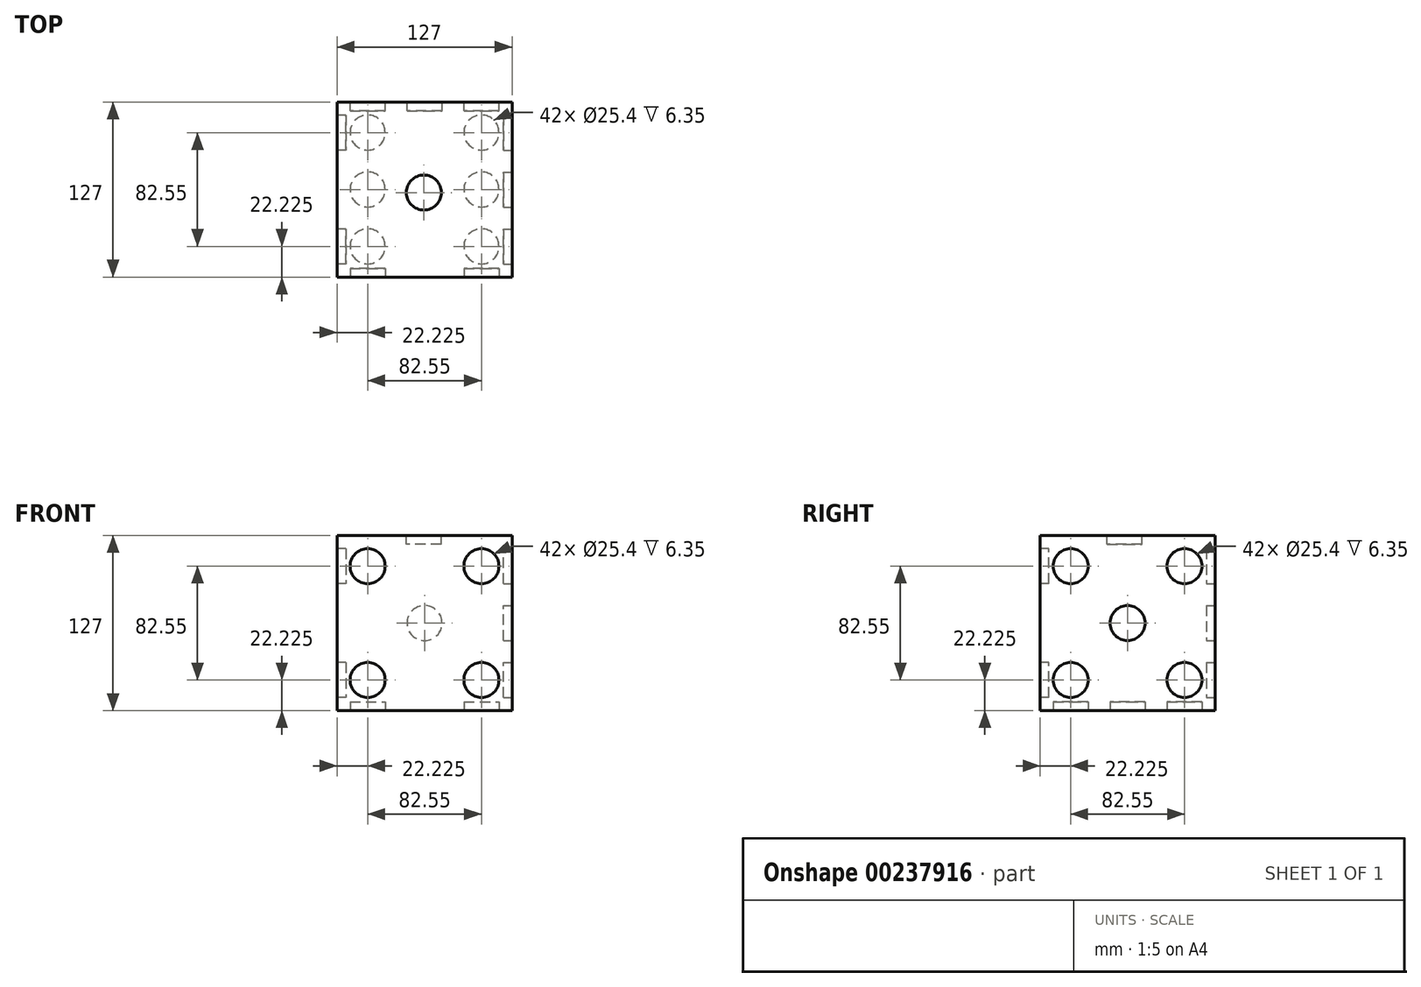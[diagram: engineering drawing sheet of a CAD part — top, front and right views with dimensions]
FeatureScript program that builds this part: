
annotation { "Feature Type Name" : "Feature", "Feature Type Description" : "" }
export const myFeature = defineFeature(function(context is Context, id is Id, definition is map)
    precondition{}
    {
        {
            var Q0;
            Q0=qCreatedBy(makeId("Top.planeOp"),FACE);
            var sketch = newSketch(context, id + "F0", { "sketchPlane" : qUnion([Q0])});
            skLineSegment(sketch, "E0.bottom", {"start": v(0, 0) * mm, "end": v(127, 0) * mm});
            skLineSegment(sketch, "E0.top", {"start": v(0, 127) * mm, "end": v(127, 127) * mm});
            skLineSegment(sketch, "E0.left", {"start": v(0, 0) * mm, "end": v(0, 127) * mm});
            skLineSegment(sketch, "E0.right", {"start": v(127, 0) * mm, "end": v(127, 127) * mm});
            skSolve(sketch);
        }
        {
            var Q0;
            Q0=makeQuery(id+"F0.imprint","IMPRINT",FACE,{"disambiguationData":[TD([[makeQuery(id+"F0.imprint","IMPRINT",EDGE,{"derivedFrom":sQuery(id+"F0.wireOp",EDGE,"E0.bottom")}),1.0]])]});
            extrude(context, id + "F1", {"entities" : qUnion([Q0]), "depth" : 127 * mm});
        }
        {
            var Q0;
            Q0=makeQuery(id+"F1.opExtrude","CAP_FACE",FACE,{"disambiguationData":[OSD([sQuery(id+"F0.wireOp",EDGE,"E0.bottom"),sQuery(id+"F0.wireOp",EDGE,"E0.top"),sQuery(id+"F0.wireOp",EDGE,"E0.left"),sQuery(id+"F0.wireOp",EDGE,"E0.right")])],"isStart":false});
            var sketch = newSketch(context, id + "F2", { "sketchPlane" : qUnion([Q0])});
            skCircle(sketch, "E1", {"center": v(63, 61.25) * mm, "radius": 12.7 * mm});
            skSolve(sketch);
        }
        {
            var Q0;
            Q0=makeQuery(id+"F2.imprint","IMPRINT",FACE,{"disambiguationData":[TD([[makeQuery(id+"F2.imprint","IMPRINT",EDGE,{"derivedFrom":sQuery(id+"F2.wireOp",EDGE,"E1")}),1.0]])]});
            extrude(context, id + "F3", {"entities" : qUnion([Q0]), "operationType" : NewBodyOperationType.REMOVE, "oppositeDirection" : true, "depth" : 6.35 * mm});
        }
        {
            var Q0;
            Q0=makeQuery(id+"F1.opExtrude","CAP_FACE",FACE,{"disambiguationData":[OSD([sQuery(id+"F0.wireOp",EDGE,"E0.bottom"),sQuery(id+"F0.wireOp",EDGE,"E0.top"),sQuery(id+"F0.wireOp",EDGE,"E0.left"),sQuery(id+"F0.wireOp",EDGE,"E0.right")])],"isStart":true});
            var sketch = newSketch(context, id + "F4", { "sketchPlane" : qUnion([Q0])});
            skLineSegment(sketch, "E2", {"start": v(63.5, 0) * mm, "end": v(63.5, -127) * mm, "construction": true});
            skLineSegment(sketch, "E3", {"start": v(0, -63.5) * mm, "end": v(127, -63.5) * mm, "construction": true});
            skCircle(sketch, "E4", {"center": v(22.23, -22.23) * mm, "radius": 12.7 * mm});
            skCircle(sketch, "E5", {"center": v(22.23, -63.5) * mm, "radius": 12.7 * mm});
            skCircle(sketch, "E6", {"center": v(104.78, -22.23) * mm, "radius": 12.7 * mm});
            skCircle(sketch, "E7", {"center": v(104.78, -63.5) * mm, "radius": 12.7 * mm});
            skCircle(sketch, "E8", {"center": v(104.78, -104.78) * mm, "radius": 12.7 * mm});
            skLineSegment(sketch, "E9", {"start": v(0, -127) * mm, "end": v(127, 0) * mm, "construction": true});
            skCircle(sketch, "E10", {"center": v(22.22, -104.78) * mm, "radius": 12.7 * mm});
            skSolve(sketch);
        }
        {
            var Q0;
            Q0=makeQuery(id+"F4.imprint","IMPRINT",FACE,{"disambiguationData":[TD([[makeQuery(id+"F4.imprint","IMPRINT",EDGE,{"derivedFrom":sQuery(id+"F4.wireOp",EDGE,"E4")}),1.0]])]});
            var Q1;
            Q1=makeQuery(id+"F4.imprint","IMPRINT",FACE,{"disambiguationData":[TD([[makeQuery(id+"F4.imprint","IMPRINT",EDGE,{"derivedFrom":sQuery(id+"F4.wireOp",EDGE,"E5")}),1.0]])]});
            var Q2;
            Q2=makeQuery(id+"F4.imprint","IMPRINT",FACE,{"disambiguationData":[TD([[makeQuery(id+"F4.imprint","IMPRINT",EDGE,{"derivedFrom":sQuery(id+"F4.wireOp",EDGE,"E10")}),1.0]])]});
            var Q3;
            Q3=makeQuery(id+"F4.imprint","IMPRINT",FACE,{"disambiguationData":[TD([[makeQuery(id+"F4.imprint","IMPRINT",EDGE,{"derivedFrom":sQuery(id+"F4.wireOp",EDGE,"E7")}),1.0]])]});
            var Q4;
            Q4=makeQuery(id+"F4.imprint","IMPRINT",FACE,{"disambiguationData":[TD([[makeQuery(id+"F4.imprint","IMPRINT",EDGE,{"derivedFrom":sQuery(id+"F4.wireOp",EDGE,"E6")}),1.0]])]});
            var Q5;
            Q5=makeQuery(id+"F4.imprint","IMPRINT",FACE,{"disambiguationData":[TD([[makeQuery(id+"F4.imprint","IMPRINT",EDGE,{"derivedFrom":sQuery(id+"F4.wireOp",EDGE,"E8")}),1.0]])]});
            extrude(context, id + "F5", {"entities" : qUnion([Q0, Q1, Q2, Q3, Q4, Q5]), "operationType" : NewBodyOperationType.REMOVE, "oppositeDirection" : true, "depth" : 6.35 * mm});
        }
        {
            var Q0;
            Q0=makeQuery(id+"F1.opExtrude","SWEPT_FACE",FACE,{"disambiguationData":[OSD([sQuery(id+"F0.wireOp",EDGE,"E0.left")])]});
            var sketch = newSketch(context, id + "F6", { "sketchPlane" : qUnion([Q0])});
            skLineSegment(sketch, "E11", {"start": v(0, 0) * mm, "end": v(-127, 127) * mm, "construction": true});
            skCircle(sketch, "E12", {"center": v(-22.23, 22.23) * mm, "radius": 12.7 * mm});
            skCircle(sketch, "E13", {"center": v(-104.78, 104.78) * mm, "radius": 12.7 * mm});
            skSolve(sketch);
        }
        {
            var Q0;
            Q0 = qSketchRegion(id + "F6", true);
            extrude(context, id + "F7", {"entities" : qUnion([Q0]), "operationType" : NewBodyOperationType.REMOVE, "oppositeDirection" : true, "depth" : 6.35 * mm});
        }
        {
            var Q0;
            Q0=makeQuery(id+"F1.opExtrude","SWEPT_FACE",FACE,{"disambiguationData":[OSD([sQuery(id+"F0.wireOp",EDGE,"E0.right")])]});
            var sketch = newSketch(context, id + "F8", { "sketchPlane" : qUnion([Q0])});
            skLineSegment(sketch, "E14", {"start": v(0, 0) * mm, "end": v(127, 127) * mm, "construction": true});
            skLineSegment(sketch, "E15", {"start": v(0, 127) * mm, "end": v(127, 0) * mm, "construction": true});
            skCircle(sketch, "E16", {"center": v(63.5, 63.5) * mm, "radius": 12.7 * mm});
            skCircle(sketch, "E17", {"center": v(22.23, 22.23) * mm, "radius": 12.7 * mm});
            skCircle(sketch, "E18", {"center": v(22.23, 104.78) * mm, "radius": 12.7 * mm});
            skCircle(sketch, "E19", {"center": v(104.78, 104.78) * mm, "radius": 12.7 * mm});
            skCircle(sketch, "E20", {"center": v(104.78, 22.23) * mm, "radius": 12.7 * mm});
            skSolve(sketch);
        }
        {
            var Q0;
            Q0=makeQuery(id+"F8.imprint","IMPRINT",FACE,{"disambiguationData":[TD([[makeQuery(id+"F8.imprint","IMPRINT",EDGE,{"derivedFrom":sQuery(id+"F8.wireOp",EDGE,"E18")}),1.0]])]});
            var Q1;
            Q1=makeQuery(id+"F8.imprint","IMPRINT",FACE,{"disambiguationData":[TD([[makeQuery(id+"F8.imprint","IMPRINT",EDGE,{"derivedFrom":sQuery(id+"F8.wireOp",EDGE,"E16")}),1.0]])]});
            var Q2;
            Q2=makeQuery(id+"F8.imprint","IMPRINT",FACE,{"disambiguationData":[TD([[makeQuery(id+"F8.imprint","IMPRINT",EDGE,{"derivedFrom":sQuery(id+"F8.wireOp",EDGE,"E17")}),1.0]])]});
            var Q3;
            Q3=makeQuery(id+"F8.imprint","IMPRINT",FACE,{"disambiguationData":[TD([[makeQuery(id+"F8.imprint","IMPRINT",EDGE,{"derivedFrom":sQuery(id+"F8.wireOp",EDGE,"E19")}),1.0]])]});
            var Q4;
            Q4=makeQuery(id+"F8.imprint","IMPRINT",FACE,{"disambiguationData":[TD([[makeQuery(id+"F8.imprint","IMPRINT",EDGE,{"derivedFrom":sQuery(id+"F8.wireOp",EDGE,"E20")}),1.0]])]});
            extrude(context, id + "F9", {"entities" : qUnion([Q0, Q1, Q2, Q3, Q4]), "operationType" : NewBodyOperationType.REMOVE, "oppositeDirection" : true, "depth" : 6.35 * mm});
        }
        {
            var Q0;
            Q0=makeQuery(id+"F1.opExtrude","SWEPT_FACE",FACE,{"disambiguationData":[OSD([sQuery(id+"F0.wireOp",EDGE,"E0.top")])]});
            var sketch = newSketch(context, id + "F10", { "sketchPlane" : qUnion([Q0])});
            skLineSegment(sketch, "E21", {"start": v(-127, 0) * mm, "end": v(0, 127) * mm});
            skCircle(sketch, "E22", {"center": v(-63.5, 63.5) * mm, "radius": 12.7 * mm});
            skCircle(sketch, "E23", {"center": v(-22.22, 104.78) * mm, "radius": 12.7 * mm});
            skCircle(sketch, "E24", {"center": v(-104.78, 22.23) * mm, "radius": 12.7 * mm});
            skSolve(sketch);
        }
        {
            var Q0;
            Q0 = qSketchRegion(id + "F10", true);
            extrude(context, id + "F11", {"entities" : qUnion([Q0]), "operationType" : NewBodyOperationType.REMOVE, "oppositeDirection" : true, "depth" : 6.35 * mm});
        }
        {
            var Q0;
            Q0=makeQuery(id+"F1.opExtrude","SWEPT_FACE",FACE,{"disambiguationData":[OSD([sQuery(id+"F0.wireOp",EDGE,"E0.bottom")])]});
            var sketch = newSketch(context, id + "F12", { "sketchPlane" : qUnion([Q0])});
            skCircle(sketch, "E25", {"center": v(22.23, 22.22) * mm, "radius": 12.7 * mm});
            skCircle(sketch, "E26", {"center": v(22.23, 104.78) * mm, "radius": 12.7 * mm});
            skCircle(sketch, "E27", {"center": v(104.78, 104.78) * mm, "radius": 12.7 * mm});
            skCircle(sketch, "E28", {"center": v(104.78, 22.22) * mm, "radius": 12.7 * mm});
            skSolve(sketch);
        }
        {
            var Q0;
            Q0 = qSketchRegion(id + "F12", true);
            extrude(context, id + "F13", {"entities" : qUnion([Q0]), "operationType" : NewBodyOperationType.REMOVE, "oppositeDirection" : true, "depth" : 6.35 * mm});
        }
    });
